# Revit family: Doors_Sliding-Doors_Krownlab_Loki_Bypassing_Stacked1
name_source: partatom
category: Doors
revit_build: Autodesk Revit 2017 (Build: 20190508_0315(x64)
units: mm (PartAtom-declared; Revit-internal decimal feet)

## family parameters
Always vertical = Yes
Cut with Voids When Loaded = No
Host = Wall
OmniClass Number = 23.30.10.00
OmniClass Title = Doors
Room Calculation Point = No
Shared = No

## types (1)
- Refer to Type Catalog
    Analytic Construction = <None>
    Assembly Code = C1020
    Bypassing Track Region = 75 1/2"
    Center Mount Note = Center Mounts are required and will automatically turn 'ON' when the bypassing track region exceeds 6 feet.  Center Mounts can be added manually when this region is shorter than 6 feet, if panel weight exceeds the maximum panel weight without Center Mount.
    Center Mount for Front Track = Yes
    Center Mounting Point = Yes
    Clnc = 1 3/4"
    Default Door Thickness = Default Thickness is 1 3/4 inches
    Description = A completely customizable sliding door system with unparalleled field adjustability. Made in the USA from high-grade stainless steel and billet aluminum.
    Door Guides = Custom site-specific door guide required for front panel. Not provided by Krownlab.
    Door Thickness Restrictions = Top Mount door panel thickness range is: 1-3/8” – 2 1/2”. Glass Mount door panel thickness range is: 3/8” – ½”.
    Edition number = 2
    Face Mount = Face Mount is not available for Loki Bypassing products
    Function = Interior
    Glass Mount = Default Thickness is 1/2 inch
    Glass Weight Calculation = 0.00 lb
    Height = 89 7/16"
    Lft_Sd_Ctrl = 3"
    Manual Panel Weight Entry = 0.00 lb
    Manufacturer = Krownlab
    Maximum Panel Weight = 225.00 lb
    Model = Loki Bypassing Stacked Door
    Mounting Point Spacing = 24"
    Operation = Sliding
    Overlap Center = 2"
    Overlap Left = 3"
    Overlap Right = 10"
    Overlap Right Note = Overlap Right Accepted
    Overlap Top = 1 1/4"
    Overlap Warning = No
    Panel Area = 25.26 ft²
    Panel Height = 83 5/8"
    Panel Material = Wood - Krownlab - Showcase Wood
    Panel Size Availability = Available
    Panel Size Restrictions = Minimum Panel Height is 20”, Minimum Panel Width is 24”.
    Panel Width = 43 1/2"
    Product Guid = 76f97f46-7ea8-410c-a3bf-36cbabb0e76b
    Product data url = https://bimobject.com
    Projection into Opening = 0"
    Rough Height = 82 3/4"
    Rough Width = 72"
    Rt_Sd_Ctrl = 3"
    Standard Glass Weights = 3/8” glass weighs ~5lb/sf. ½” glass weighs ~6.5lb/sf
    Standoff 1 = Krownlab Track Standoff : Solid Wall - 1/4"
    Standoff 2 = Krownlab Track Standoff : Solid Wall - 1"
    Thickness = 1 3/4"
    Thickness Control = 1 3/4"
    Top Mount = Default Thickness is 1 3/4 inches
    Track Length = 118 1/2"
    Track Mounting Note = Track mounting point pattern is approximate, and will differ from actual requirements of system.  Maximum single length track is 142”. Multiple tracks can be connected.  Please contact manufacturer for more information.
    Trk_Stp = 2 1/8"
    Trolley Distance From Panel Edge = 3"
    URL = www.krownlab.com/loki
    Wall Closure = By host
    |_Mt_Opt_01 = Yes
    |_Mt_Opt_02 = No
    |_Pn_Opt_01 = Yes
    |_Pn_Opt_02 = No

## geometry (parser evidence)
native form markers: Sweep x17
no freeform markers — native parametric forms only
